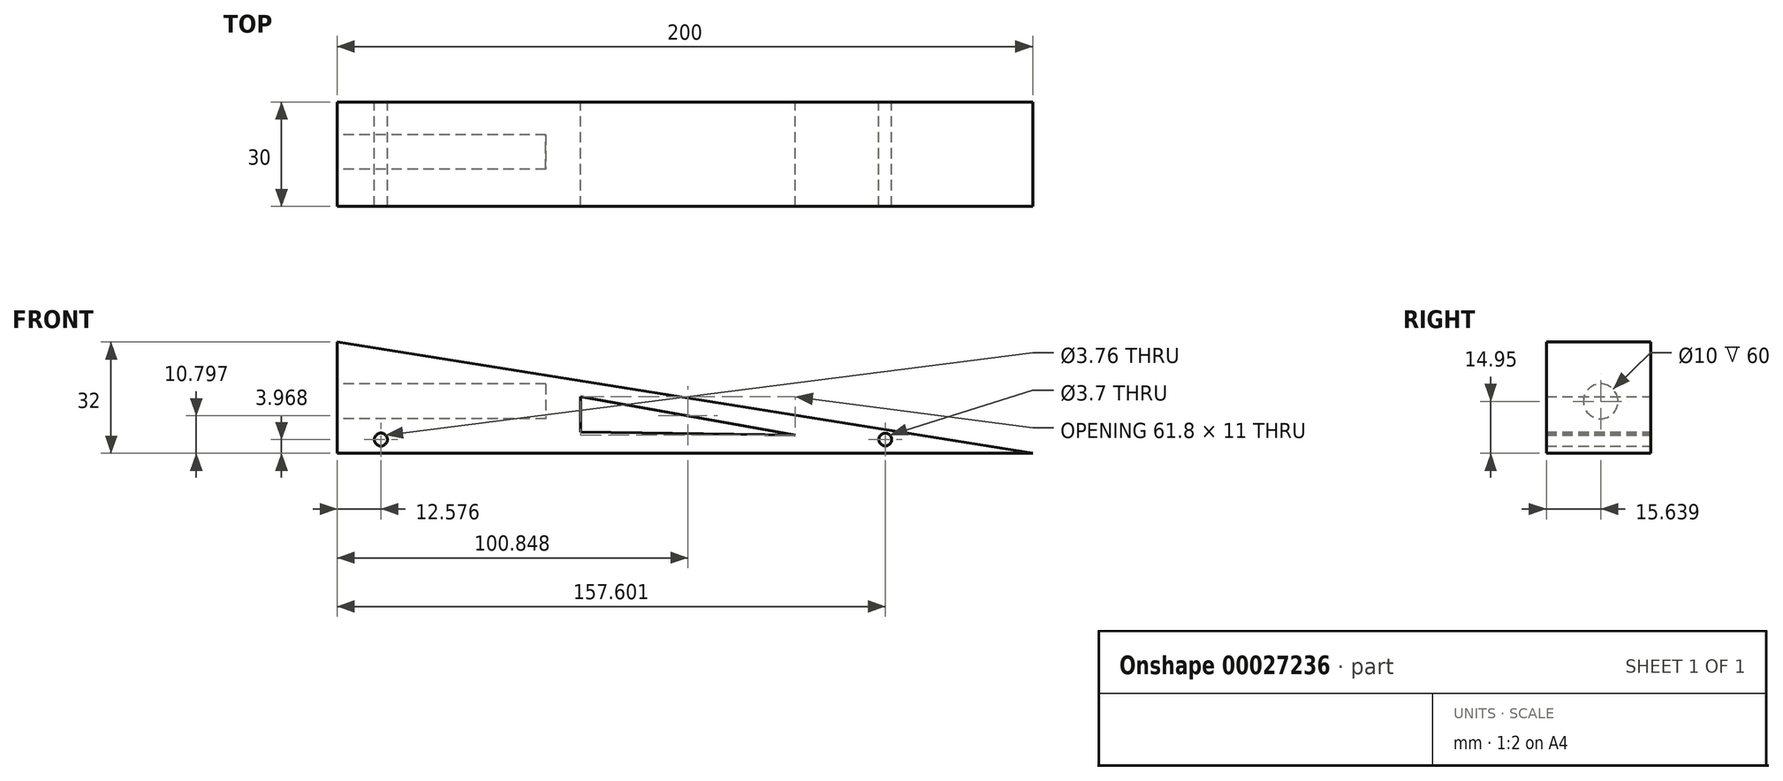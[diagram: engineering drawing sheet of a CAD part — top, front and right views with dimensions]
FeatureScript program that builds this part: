
annotation { "Feature Type Name" : "Feature", "Feature Type Description" : "" }
export const myFeature = defineFeature(function(context is Context, id is Id, definition is map)
    precondition{}
    {
        {
            var Q0;
            Q0=qCreatedBy(makeId("Front.planeOp"),FACE);
            var sketch = newSketch(context, id + "F0", { "sketchPlane" : qUnion([Q0])});
            skLineSegment(sketch, "E0", {"start": v(-131.75, 0) * mm, "end": v(68.25, 0) * mm});
            skLineSegment(sketch, "E1", {"start": v(68.25, 0) * mm, "end": v(-131.75, 32) * mm});
            skLineSegment(sketch, "E2", {"start": v(-131.75, 32) * mm, "end": v(-131.75, 0) * mm});
            skCircle(sketch, "E3", {"center": v(-119.17, 3.97) * mm, "radius": 1.88 * mm});
            skCircle(sketch, "E4", {"center": v(25.85, 3.97) * mm, "radius": 1.85 * mm});
            skSolve(sketch);
        }
        {
            var Q0;
            Q0=makeQuery(id+"F0.imprint","IMPRINT",FACE,{"disambiguationData":[TD([[makeQuery(id+"F0.imprint","IMPRINT",EDGE,{"derivedFrom":sQuery(id+"F0.wireOp",EDGE,"E0")}),1.0]])]});
            extrude(context, id + "F1", {"entities" : qUnion([Q0]), "depth" : 30 * mm});
        }
        {
            var Q0;
            Q0=makeQuery(id+"F1.opExtrude","SWEPT_FACE",FACE,{"disambiguationData":[OSD([sQuery(id+"F0.wireOp",EDGE,"E2")])]});
            var sketch = newSketch(context, id + "F2", { "sketchPlane" : qUnion([Q0])});
            skCircle(sketch, "E5", {"center": v(14.36, 14.95) * mm, "radius": 5 * mm});
            skSolve(sketch);
        }
        {
            var Q0;
            Q0=makeQuery(id+"F2.imprint","IMPRINT",FACE,{"disambiguationData":[TD([[makeQuery(id+"F2.imprint","IMPRINT",EDGE,{"derivedFrom":sQuery(id+"F2.wireOp",EDGE,"E5")}),1.0]])]});
            extrude(context, id + "F3", {"entities" : qUnion([Q0]), "operationType" : NewBodyOperationType.REMOVE, "oppositeDirection" : true, "depth" : 60 * mm});
        }
        {
            var Q0;
            Q0=qCreatedBy(makeId("Front.planeOp"),FACE);
            var sketch = newSketch(context, id + "F4", { "sketchPlane" : qUnion([Q0])});
            skLineSegment(sketch, "E6", {"start": v(-61.8, 6.17) * mm, "end": v(-61.8, 16.3) * mm});
            skLineSegment(sketch, "E7", {"start": v(-61.8, 16.3) * mm, "end": v(0, 5.3) * mm});
            skLineSegment(sketch, "E8", {"start": v(0, 5.3) * mm, "end": v(-61.8, 6.17) * mm});
            skSolve(sketch);
        }
        {
            var Q0;
            Q0=makeQuery(id+"F4.imprint","IMPRINT",FACE,{"disambiguationData":[TD([[makeQuery(id+"F4.imprint","IMPRINT",EDGE,{"derivedFrom":sQuery(id+"F4.wireOp",EDGE,"E6")}),-1.0]])]});
            extrude(context, id + "F5", {"entities" : qUnion([Q0]), "operationType" : NewBodyOperationType.REMOVE, "endBound" : BoundingType.THROUGH_ALL, "depth" : 25 * mm});
        }
    });
